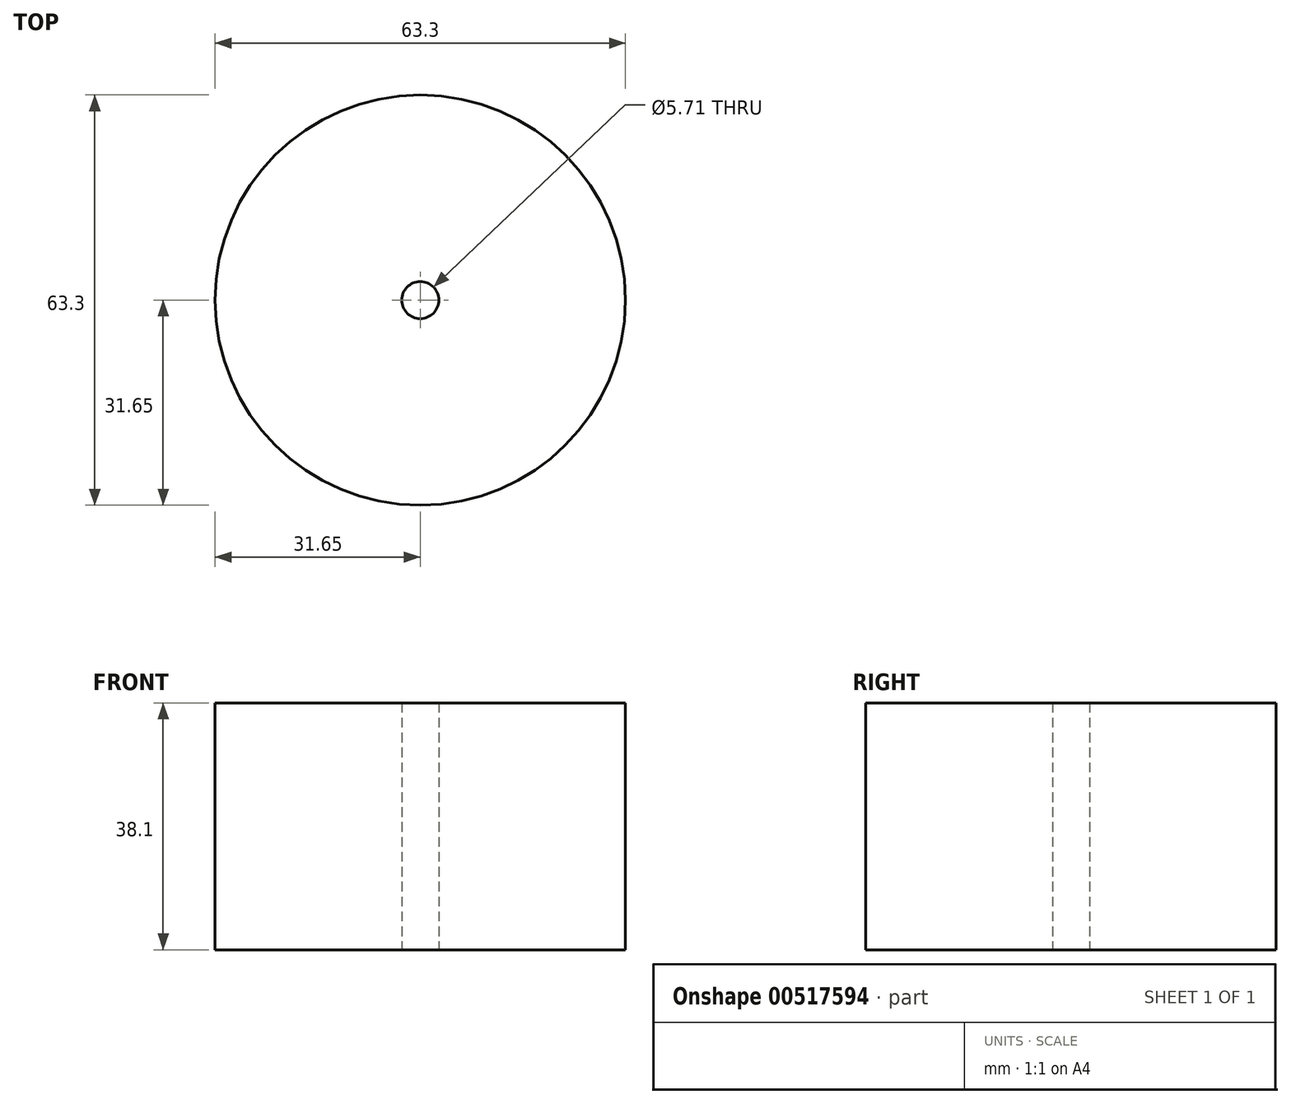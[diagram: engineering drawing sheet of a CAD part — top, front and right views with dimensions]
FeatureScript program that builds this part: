
annotation { "Feature Type Name" : "Feature", "Feature Type Description" : "" }
export const myFeature = defineFeature(function(context is Context, id is Id, definition is map)
    precondition{}
    {
        {
            var Q0;
            Q0=qCreatedBy(makeId("Top.planeOp"),FACE);
            var sketch = newSketch(context, id + "F0", { "sketchPlane" : qUnion([Q0])});
            skCircle(sketch, "E0", {"center": v(0, 0) * mm, "radius": 31.65 * mm});
            skCircle(sketch, "E1", {"center": v(0, 0) * mm, "radius": 16.29 * mm});
            skCircle(sketch, "E2", {"center": v(0, 0) * mm, "radius": 2.85 * mm});
            skSolve(sketch);
        }
        {
            var Q0;
            Q0 = qSketchRegion(id + "F0", true);
            var Q1;
            Q1=makeQuery(id+"F0.imprint","IMPRINT",FACE,{"disambiguationData":[TD([[makeQuery(id+"F0.imprint","IMPRINT",EDGE,{"derivedFrom":sQuery(id+"F0.wireOp",EDGE,"E1")}),1.0]])]});
            extrude(context, id + "F1", {"entities" : qUnion([Q0, Q1]), "depth" : 5.08 * mm, "offsetDistance" : 25.4 * mm});
        }
        {
            var Q0;
            Q0=makeQuery(id+"F1.opExtrude","CAP_FACE",FACE,{"disambiguationData":[OSD([sQuery(id+"F0.wireOp",EDGE,"E0"),sQuery(id+"F0.wireOp",EDGE,"E2")])],"isStart":false});
            extrude(context, id + "F2", {"entities" : qUnion([Q0]), "operationType" : NewBodyOperationType.ADD, "depth" : 25.4 * mm, "offsetDistance" : 25.4 * mm});
        }
        {
            var Q0;
            Q0 = qSketchRegion(id + "F0", true);
            var Q1;
            Q1=makeQuery(id+"F2.opExtrude","CAP_FACE",FACE,{"disambiguationData":[OSD([sQuery(id+"F0.wireOp",EDGE,"E0"),sQuery(id+"F0.wireOp",EDGE,"E2")])],"isStart":false});
            extrude(context, id + "F3", {"entities" : qUnion([Q0, Q1]), "operationType" : NewBodyOperationType.ADD, "depth" : 7.62 * mm, "offsetDistance" : 25.4 * mm});
        }
    });
